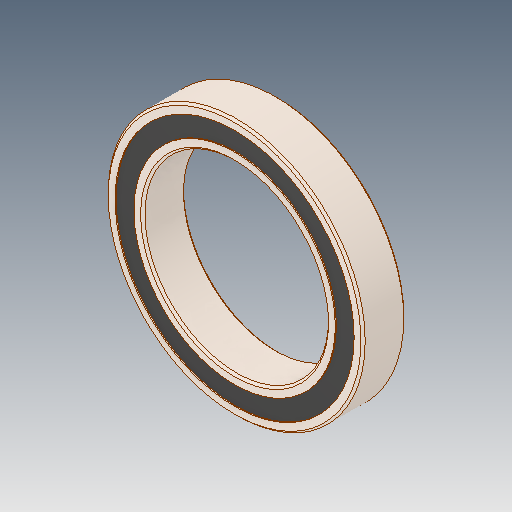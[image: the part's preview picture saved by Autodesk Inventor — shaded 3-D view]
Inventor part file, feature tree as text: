
AUTODESK INVENTOR PART (.ipt)
format: ipt  version: 2019 (Build 230136000, 136)  size: 583,168 bytes
history: native  units: mm
features: other x11, revolve x5
ambient origin geometry x8: Origin, YZ Plane, XZ Plane, XY Plane, X Axis, Y Axis, Z Axis, Center Point
bodies: Solid1 (feature_tree), Solid2 (feature_tree), Solid3 (feature_tree), Solid4 (feature_tree), Solid5 (feature_tree), Solid6 (feature_tree), Solid7 (feature_tree), Solid8 (feature_tree), Solid9 (feature_tree), Solid10 (feature_tree), Solid11 (feature_tree), Solid12 (feature_tree), Solid13 (feature_tree), Solid14 (feature_tree), Solid15 (feature_tree), Solid16 (feature_tree)
feature tree (16):
  revolve  "Revolve1"  [1 undecoded]
  revolve  "Revolve3"  [1 undecoded]
  revolve  "Revolve4"  [1 undecoded]
  other  "CirPattern1[1]"
  other  "CirPattern1[2]"
  other  "CirPattern1[3]"
  other  "CirPattern1[4]"
  other  "CirPattern1[5]"
  other  "CirPattern1[6]"
  other  "CirPattern1[7]"
  other  "CirPattern1[8]"
  other  "CirPattern1[9]"
  other  "CirPattern1[10]"
  other  "CirPattern1[11]"
  revolve  "Revolve5[1]"  [1 undecoded]
  revolve  "Revolve5[2]"  [1 undecoded]
note: 5 required parameter values undecoded (feature->parameter linkage not recoverable at this tier; creation-order binding heuristic only, values carry confidence <= 0.55)
